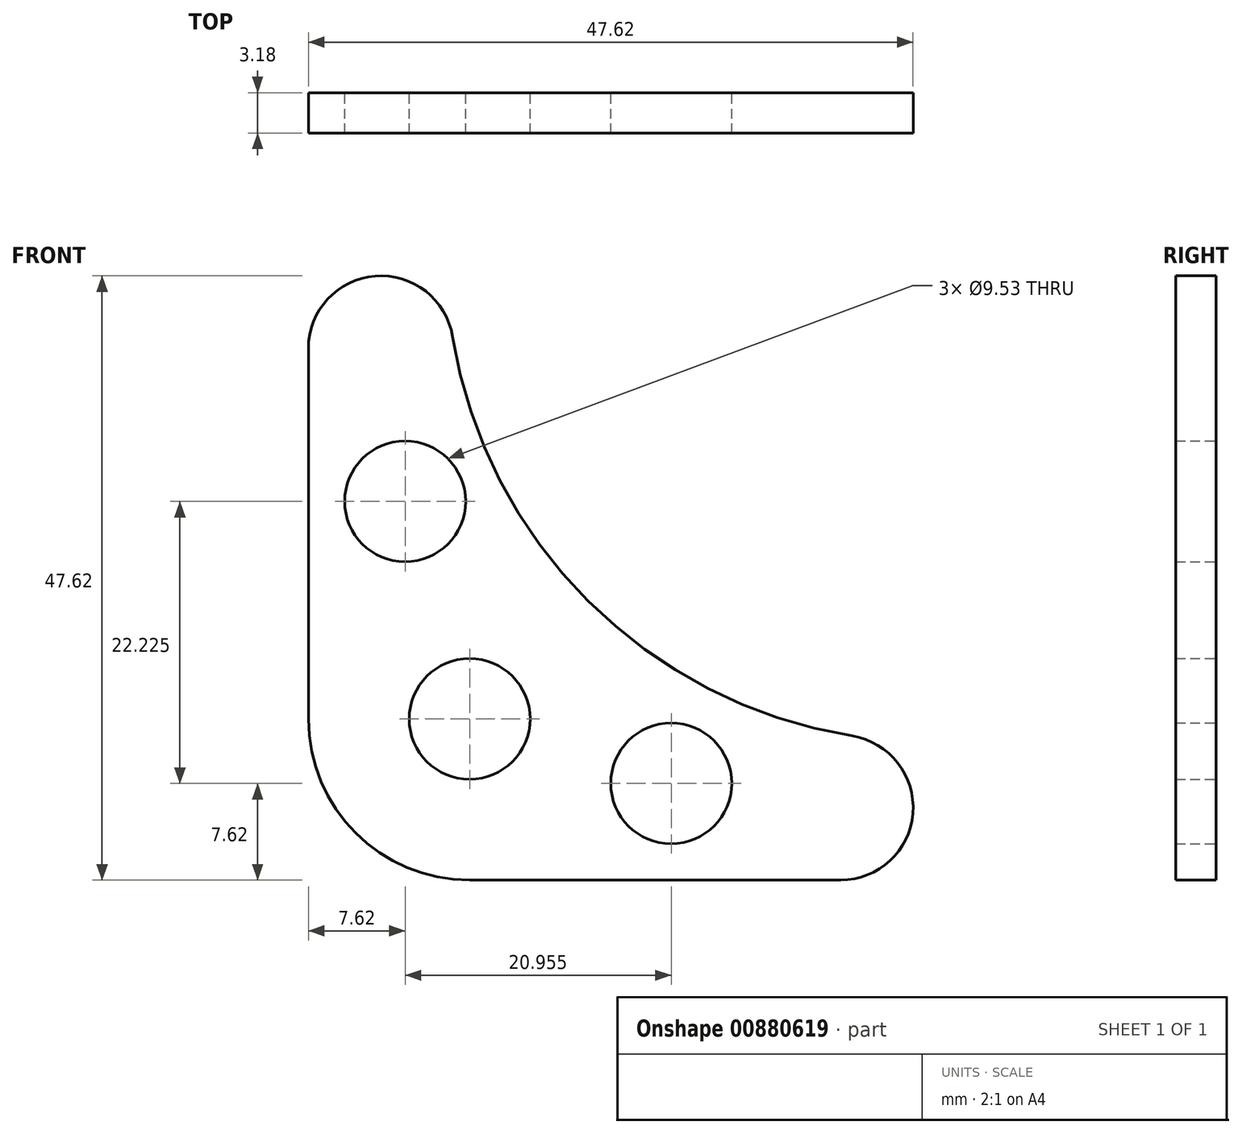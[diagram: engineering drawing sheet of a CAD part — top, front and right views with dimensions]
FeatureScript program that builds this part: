
annotation { "Feature Type Name" : "Feature", "Feature Type Description" : "" }
export const myFeature = defineFeature(function(context is Context, id is Id, definition is map)
    precondition{}
    {
        {
            var Q0;
            Q0=qCreatedBy(makeId("Front.planeOp"),FACE);
            var sketch = newSketch(context, id + "F0", { "sketchPlane" : qUnion([Q0])});
            skArc(sketch, "E0", {"start": v(11.36, 42.83) * mm, "mid": v(5.25, 47.6) * mm, "end": v(0, 41.91) * mm});
            skArc(sketch, "E1", {"start": v(41.91, 0) * mm, "mid": v(47.6, 5.25) * mm, "end": v(42.83, 11.36) * mm});
            skArc(sketch, "E2", {"start": v(11.36, 42.83) * mm, "mid": v(22.02, 22.02) * mm, "end": v(42.83, 11.36) * mm});
            skLineSegment(sketch, "E3", {"start": v(41.91, 0) * mm, "end": v(12.7, 0) * mm});
            skLineSegment(sketch, "E4", {"start": v(0, 12.7) * mm, "end": v(0, 41.91) * mm});
            skPoint(sketch, "E5.visualSharp", {"position": v(0, 0) * mm});
            skArc(sketch, "E5.filletArc", {"start": v(0, 12.7) * mm, "mid": v(3.72, 3.72) * mm, "end": v(12.7, 0) * mm});
            skCircle(sketch, "E6", {"center": v(12.7, 12.7) * mm, "radius": 4.76 * mm});
            skCircle(sketch, "E7", {"center": v(28.58, 7.62) * mm, "radius": 4.76 * mm});
            skCircle(sketch, "E8", {"center": v(7.62, 29.85) * mm, "radius": 4.76 * mm});
            skSolve(sketch);
        }
        {
            var Q0;
            Q0 = qSketchRegion(id + "F0", true);
            extrude(context, id + "F1", {"entities" : qUnion([Q0]), "depth" : 3.17 * mm, "offsetDistance" : 25.4 * mm});
        }
    });
